# Revit family: 201_DINO-A-_x_
name_source: partatom
category: Air Terminals
units: mm (PartAtom-declared; Revit-internal decimal feet)

## family parameters
Always vertical = Yes
Cut with Voids When Loaded = No
Part Type = Normal
Room Calculation Point = Yes
Round Connector Dimension = Use Diameter
Shared = No
Work Plane-Based = No

## types (4) — shared parameters
B2 = 200 mm  [stored 0.656168 ft]
CAT0 = Yes
CAT1 = No
CAT2 = No
D = 160 mm  [stored 0.524934 ft]
D2 = 192 mm  [stored 0.629921 ft]
Description = Surface mounted Displacement device
E = 100 mm  [stored 0.328084 ft]
G = 355 mm  [stored 1.1647 ft]
H1 = 85 mm  [stored 0.278871 ft]
H3 = 600 mm  [stored 1.9685 ft]
H5 = 178 mm
I = 160 mm  [stored 0.524934 ft]
L1 = 55 mm  [stored 0.180446 ft]
L1__ve = -55 mm  [stored -0.180446 ft]
L_ARR = 400 mm  [stored 1.31234 ft]
Manufacturer = Climecon
OSA1 = Yes
OSA2 = No
OSA3 = No
R = 80 mm  [stored 0.262467 ft]
URL = www.climecon.fi
W_ARR = 400 mm  [stored 1.31234 ft]
X1 = 55 mm  [stored 0.180446 ft]
XRefLineVPlnId = 7453
YRefLineVPlnId = 7456
magiPartTypeId = 201
magiProductFamilyId = DINO-A-*x*
zero-valued in all types: H_ARR, MC_Default_elevation

## per-type parameters (varying)
| type | A1 | A2 | A3 | B | B3 | BB | C | CLBTZ | CL_Location_5000 | H | H2 | H4 | H7 | R1 | R2 | R3 | X2 | X3 |
| DINO-A-300x60 | 320 mm  [stored 1.04987 ft] | 160 mm  [stored 0.524934 ft] | 360 mm  [stored 1.1811 ft] | 300 mm | 150 mm  [stored 0.492126 ft] | 400 mm  [stored 1.31234 ft] | 200 mm  [stored 0.656168 ft] | 1185 mm | 6185 mm | 60 mm | 485 mm  [stored 1.59121 ft] | 1085 mm | 1185 mm | 160 mm  [stored 0.524934 ft] | 47 mm | 59 mm | 115 mm  [stored 0.377297 ft] | 85 mm  [stored 0.278871 ft] |
| DINO-A-1000x200 | 960 mm | 610 mm  [stored 2.00131 ft] | 1000 mm | 1000 mm | 500 mm  [stored 1.64042 ft] | 1400 mm | 390 mm  [stored 1.27953 ft] | 2185 mm | 7185 mm | 200 mm | 1485 mm | 2085 mm | 2185 mm | 350 mm  [stored 1.14829 ft] | 103 mm | 114 mm | 255 mm  [stored 0.836614 ft] | 155 mm  [stored 0.50853 ft] |
| DINO-A-700x150 | 660 mm | 400 mm  [stored 1.31234 ft] | 700 mm | 700 mm | 350 mm  [stored 1.14829 ft] | 1000 mm | 300 mm  [stored 0.984252 ft] | 1785 mm | 6785 mm | 150 mm | 1085 mm | 1685 mm | 1785 mm | 260 mm  [stored 0.853018 ft] | 76 mm | 88 mm | 205 mm  [stored 0.672572 ft] | 130 mm  [stored 0.426509 ft] |
| DINO-A-400x100 | 460 mm  [stored 1.50919 ft] | 250 mm  [stored 0.82021 ft] | 500 mm  [stored 1.64042 ft] | 400 mm | 200 mm  [stored 0.656168 ft] | 600 mm  [stored 1.9685 ft] | 250 mm  [stored 0.82021 ft] | 1385 mm | 6385 mm | 100 mm | 685 mm | 1285 mm | 1385 mm | 210 mm  [stored 0.688976 ft] | 62 mm | 73 mm | 155 mm  [stored 0.50853 ft] | 105 mm  [stored 0.344488 ft] |

note: column(s) folded — value = type name in every type: magiProductCode, magiProductId

note: [stored X ft] marks values corroborated as IEEE doubles in the binary element streams (Revit-internal decimal feet)

## geometry (parser evidence)
native form markers: Sweep x1
no freeform markers — native parametric forms only
